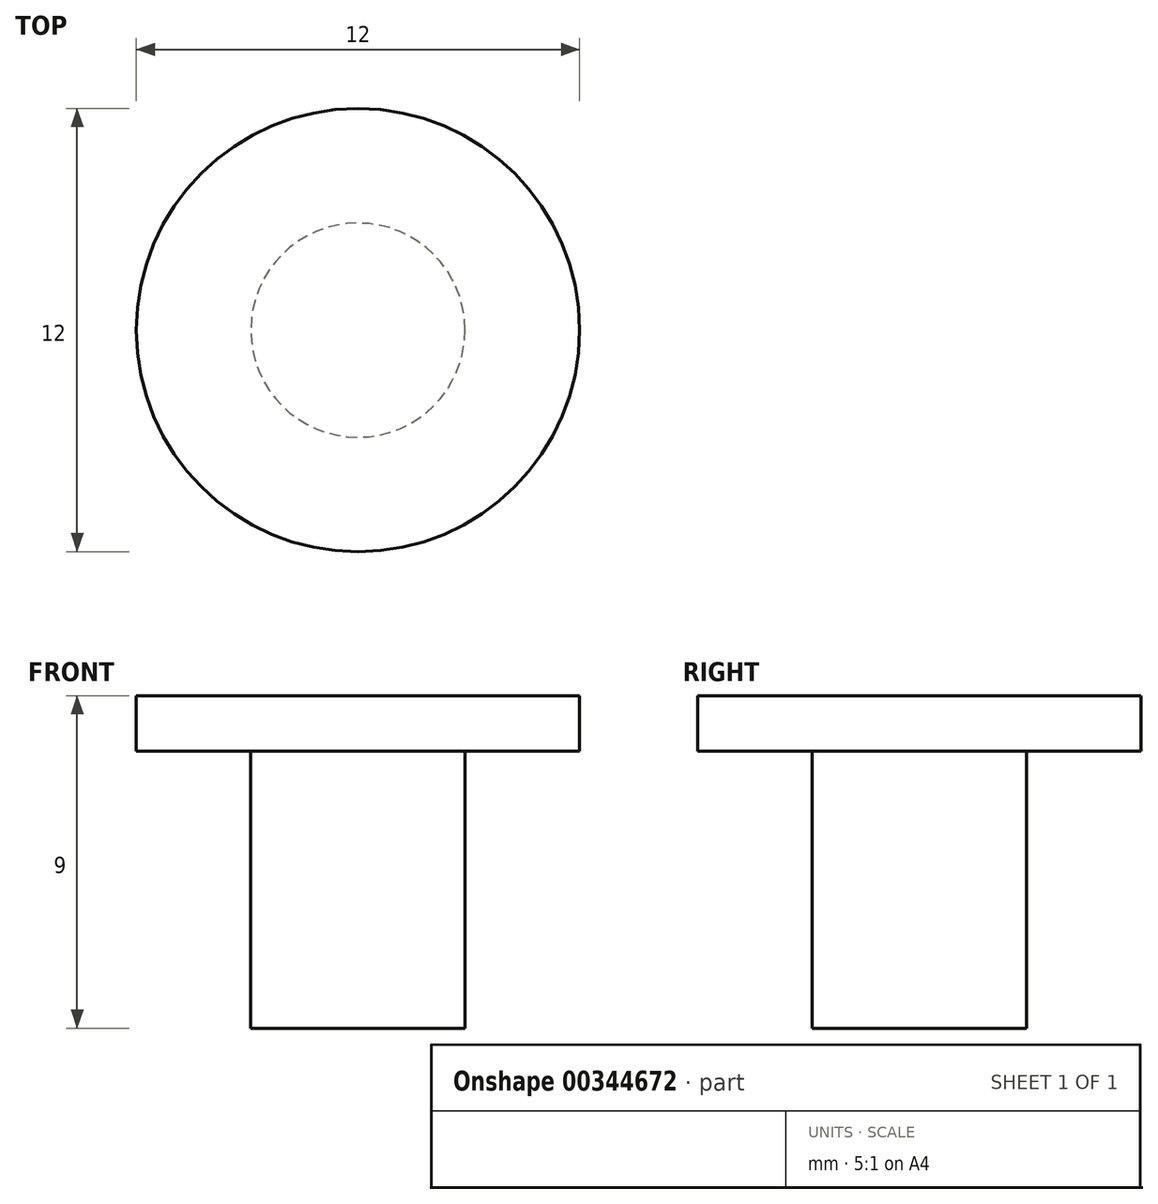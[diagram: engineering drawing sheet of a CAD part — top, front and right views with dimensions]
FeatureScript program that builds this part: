
annotation { "Feature Type Name" : "Feature", "Feature Type Description" : "" }
export const myFeature = defineFeature(function(context is Context, id is Id, definition is map)
    precondition{}
    {
        {
            var Q0;
            Q0=qCreatedBy(makeId("Top.planeOp"),FACE);
            var sketch = newSketch(context, id + "F0", { "sketchPlane" : qUnion([Q0])});
            skCircle(sketch, "E0", {"center": v(0, 0) * mm, "radius": 2.9 * mm});
            skCircle(sketch, "E1", {"center": v(0, 0) * mm, "radius": 6 * mm});
            skSolve(sketch);
        }
        {
            var Q0;
            Q0=makeQuery(id+"F0.imprint","IMPRINT",FACE,{"disambiguationData":[TD([[makeQuery(id+"F0.imprint","IMPRINT",EDGE,{"derivedFrom":sQuery(id+"F0.wireOp",EDGE,"E0")}),1.0]])]});
            extrude(context, id + "F1", {"entities" : qUnion([Q0]), "oppositeDirection" : true, "depth" : 7.5 * mm});
        }
        {
            var Q0;
            Q0=makeQuery(id+"F0.imprint","IMPRINT",FACE,{"disambiguationData":[TD([[makeQuery(id+"F0.imprint","IMPRINT",EDGE,{"derivedFrom":sQuery(id+"F0.wireOp",EDGE,"E0")}),-1.0]])]});
            var Q1;
            Q1=makeQuery(id+"F0.imprint","IMPRINT",FACE,{"disambiguationData":[TD([[makeQuery(id+"F0.imprint","IMPRINT",EDGE,{"derivedFrom":sQuery(id+"F0.wireOp",EDGE,"E0")}),1.0]])]});
            extrude(context, id + "F2", {"entities" : qUnion([Q0, Q1]), "operationType" : NewBodyOperationType.ADD, "depth" : 1.5 * mm});
        }
    });
